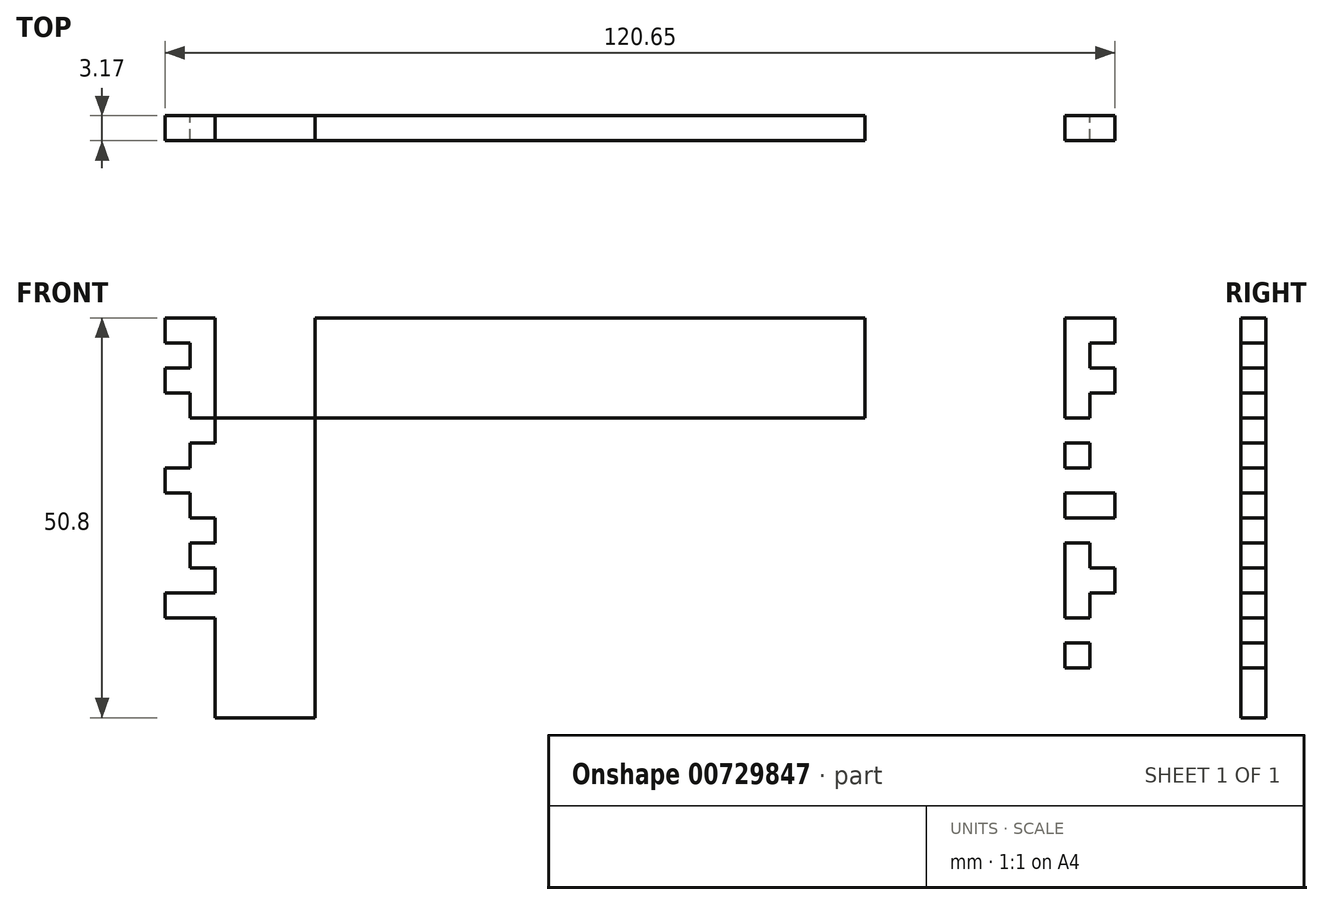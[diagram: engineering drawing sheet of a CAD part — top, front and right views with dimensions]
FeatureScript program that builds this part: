
annotation { "Feature Type Name" : "Feature", "Feature Type Description" : "" }
export const myFeature = defineFeature(function(context is Context, id is Id, definition is map)
    precondition{}
    {
        {
            var Q0;
            Q0=qCreatedBy(makeId("Front.planeOp"),FACE);
            var sketch = newSketch(context, id + "F0", { "sketchPlane" : qUnion([Q0])});
            skLineSegment(sketch, "E0.bottom", {"start": v(-86.22, 48.2) * mm, "end": v(34.43, 48.2) * mm});
            skLineSegment(sketch, "E0.top", {"start": v(-86.22, -2.6) * mm, "end": v(34.43, -2.6) * mm});
            skLineSegment(sketch, "E0.left", {"start": v(-86.22, 48.2) * mm, "end": v(-86.22, -2.6) * mm});
            skLineSegment(sketch, "E0.right", {"start": v(34.43, 48.2) * mm, "end": v(34.43, -2.6) * mm});
            skLineSegment(sketch, "E1.bottom", {"start": v(-86.22, 48.2) * mm, "end": v(-79.87, 48.2) * mm});
            skLineSegment(sketch, "E1.top", {"start": v(-86.22, -2.6) * mm, "end": v(-79.87, -2.6) * mm});
            skLineSegment(sketch, "E1.right", {"start": v(-79.87, 48.2) * mm, "end": v(-79.87, -2.6) * mm});
            skLineSegment(sketch, "E2.bottom", {"start": v(34.43, 48.2) * mm, "end": v(28.08, 48.2) * mm});
            skLineSegment(sketch, "E2.top", {"start": v(34.43, -2.6) * mm, "end": v(28.08, -2.6) * mm});
            skLineSegment(sketch, "E2.right", {"start": v(28.08, 48.2) * mm, "end": v(28.08, -2.6) * mm});
            skLineSegment(sketch, "E3.top", {"start": v(34.43, 41.85) * mm, "end": v(28.08, 41.85) * mm});
            skLineSegment(sketch, "E3.left", {"start": v(34.43, 48.2) * mm, "end": v(34.43, 41.85) * mm});
            skLineSegment(sketch, "E3.right", {"start": v(28.08, 48.2) * mm, "end": v(28.08, 41.85) * mm});
            skLineSegment(sketch, "E4.top", {"start": v(34.43, 35.5) * mm, "end": v(28.08, 35.5) * mm});
            skLineSegment(sketch, "E4.left", {"start": v(34.43, 48.2) * mm, "end": v(34.43, 35.5) * mm});
            skLineSegment(sketch, "E4.right", {"start": v(28.08, 48.2) * mm, "end": v(28.08, 35.5) * mm});
            skLineSegment(sketch, "E5.top", {"start": v(34.43, 22.8) * mm, "end": v(28.08, 22.8) * mm});
            skLineSegment(sketch, "E5.left", {"start": v(34.43, 48.2) * mm, "end": v(34.43, 22.8) * mm});
            skLineSegment(sketch, "E5.right", {"start": v(28.08, 48.2) * mm, "end": v(28.08, 22.8) * mm});
            skLineSegment(sketch, "E6.top", {"start": v(34.43, 16.45) * mm, "end": v(28.08, 16.45) * mm});
            skLineSegment(sketch, "E6.left", {"start": v(34.43, 48.2) * mm, "end": v(34.43, 16.45) * mm});
            skLineSegment(sketch, "E6.right", {"start": v(28.08, 48.2) * mm, "end": v(28.08, 16.45) * mm});
            skLineSegment(sketch, "E7.top", {"start": v(34.43, 10.1) * mm, "end": v(28.08, 10.1) * mm});
            skLineSegment(sketch, "E7.left", {"start": v(34.43, 48.2) * mm, "end": v(34.43, 10.1) * mm});
            skLineSegment(sketch, "E7.right", {"start": v(28.08, 48.2) * mm, "end": v(28.08, 10.1) * mm});
            skLineSegment(sketch, "E8.top", {"start": v(34.43, 3.75) * mm, "end": v(28.08, 3.75) * mm});
            skLineSegment(sketch, "E8.left", {"start": v(34.43, 48.2) * mm, "end": v(34.43, 3.75) * mm});
            skLineSegment(sketch, "E8.right", {"start": v(28.08, 48.2) * mm, "end": v(28.08, 3.75) * mm});
            skLineSegment(sketch, "E9.bottom", {"start": v(28.08, 48.2) * mm, "end": v(34.43, 48.2) * mm});
            skLineSegment(sketch, "E9.top", {"start": v(28.08, 29.15) * mm, "end": v(34.43, 29.15) * mm});
            skLineSegment(sketch, "E9.left", {"start": v(28.08, 48.2) * mm, "end": v(28.08, 29.15) * mm});
            skLineSegment(sketch, "E9.right", {"start": v(34.43, 48.2) * mm, "end": v(34.43, 29.15) * mm});
            skLineSegment(sketch, "E10.top", {"start": v(-86.22, 41.85) * mm, "end": v(-79.87, 41.85) * mm});
            skLineSegment(sketch, "E10.left", {"start": v(-86.22, 48.2) * mm, "end": v(-86.22, 41.85) * mm});
            skLineSegment(sketch, "E10.right", {"start": v(-79.87, 48.2) * mm, "end": v(-79.87, 41.85) * mm});
            skLineSegment(sketch, "E11.top", {"start": v(-86.22, 35.5) * mm, "end": v(-79.87, 35.5) * mm});
            skLineSegment(sketch, "E11.left", {"start": v(-86.22, 48.2) * mm, "end": v(-86.22, 35.5) * mm});
            skLineSegment(sketch, "E11.right", {"start": v(-79.87, 48.2) * mm, "end": v(-79.87, 35.5) * mm});
            skLineSegment(sketch, "E12.top", {"start": v(-86.22, 3.75) * mm, "end": v(-79.87, 3.75) * mm});
            skLineSegment(sketch, "E12.left", {"start": v(-86.22, 48.2) * mm, "end": v(-86.22, 3.75) * mm});
            skLineSegment(sketch, "E12.right", {"start": v(-79.87, 48.2) * mm, "end": v(-79.87, 3.75) * mm});
            skLineSegment(sketch, "E13.top", {"start": v(-86.22, 10.1) * mm, "end": v(-79.87, 10.1) * mm});
            skLineSegment(sketch, "E13.left", {"start": v(-86.22, 48.2) * mm, "end": v(-86.22, 10.1) * mm});
            skLineSegment(sketch, "E13.right", {"start": v(-79.87, 48.2) * mm, "end": v(-79.87, 10.1) * mm});
            skLineSegment(sketch, "E14.top", {"start": v(-86.22, 29.15) * mm, "end": v(-79.87, 29.15) * mm});
            skLineSegment(sketch, "E14.left", {"start": v(-86.22, 48.2) * mm, "end": v(-86.22, 29.15) * mm});
            skLineSegment(sketch, "E14.right", {"start": v(-79.87, 48.2) * mm, "end": v(-79.87, 29.15) * mm});
            skLineSegment(sketch, "E15.top", {"start": v(-86.22, 22.8) * mm, "end": v(-79.87, 22.8) * mm});
            skLineSegment(sketch, "E15.left", {"start": v(-86.22, 48.2) * mm, "end": v(-86.22, 22.8) * mm});
            skLineSegment(sketch, "E15.right", {"start": v(-79.87, 48.2) * mm, "end": v(-79.87, 22.8) * mm});
            skLineSegment(sketch, "E16.top", {"start": v(-86.22, 16.45) * mm, "end": v(-79.87, 16.45) * mm});
            skLineSegment(sketch, "E16.left", {"start": v(-86.22, 48.2) * mm, "end": v(-86.22, 16.45) * mm});
            skLineSegment(sketch, "E16.right", {"start": v(-79.87, 48.2) * mm, "end": v(-79.87, 16.45) * mm});
            skLineSegment(sketch, "E17", {"start": v(-79.87, 48.2) * mm, "end": v(-67.17, 48.2) * mm});
            skLineSegment(sketch, "E18", {"start": v(-67.17, 48.2) * mm, "end": v(-67.17, -2.6) * mm});
            skLineSegment(sketch, "E19", {"start": v(-86.22, 35.5) * mm, "end": v(34.43, 35.5) * mm});
            skLineSegment(sketch, "E20.bottom", {"start": v(-86.22, 48.2) * mm, "end": v(-83.05, 48.2) * mm});
            skLineSegment(sketch, "E20.top", {"start": v(-86.22, -2.6) * mm, "end": v(-83.05, -2.6) * mm});
            skLineSegment(sketch, "E20.right", {"start": v(-83.05, 48.2) * mm, "end": v(-83.05, -2.6) * mm});
            skLineSegment(sketch, "E21.bottom", {"start": v(-79.87, 48.2) * mm, "end": v(-86.22, 48.2) * mm});
            skLineSegment(sketch, "E21.top", {"start": v(-79.87, 45.02) * mm, "end": v(-86.22, 45.02) * mm});
            skLineSegment(sketch, "E21.left", {"start": v(-79.87, 48.2) * mm, "end": v(-79.87, 45.02) * mm});
            skLineSegment(sketch, "E21.right", {"start": v(-86.22, 48.2) * mm, "end": v(-86.22, 45.02) * mm});
            skLineSegment(sketch, "E22.bottom", {"start": v(-79.87, 41.85) * mm, "end": v(-86.22, 41.85) * mm});
            skLineSegment(sketch, "E22.top", {"start": v(-79.87, 38.67) * mm, "end": v(-86.22, 38.67) * mm});
            skLineSegment(sketch, "E22.left", {"start": v(-79.87, 41.85) * mm, "end": v(-79.87, 38.67) * mm});
            skLineSegment(sketch, "E22.right", {"start": v(-86.22, 41.85) * mm, "end": v(-86.22, 38.67) * mm});
            skLineSegment(sketch, "E23.bottom", {"start": v(-79.87, 35.5) * mm, "end": v(-86.22, 35.5) * mm});
            skLineSegment(sketch, "E23.top", {"start": v(-79.87, 32.32) * mm, "end": v(-86.22, 32.32) * mm});
            skLineSegment(sketch, "E23.left", {"start": v(-79.87, 35.5) * mm, "end": v(-79.87, 32.32) * mm});
            skLineSegment(sketch, "E23.right", {"start": v(-86.22, 35.5) * mm, "end": v(-86.22, 32.32) * mm});
            skLineSegment(sketch, "E24.bottom", {"start": v(-79.87, 29.15) * mm, "end": v(-86.22, 29.15) * mm});
            skLineSegment(sketch, "E24.top", {"start": v(-79.87, 25.97) * mm, "end": v(-86.22, 25.97) * mm});
            skLineSegment(sketch, "E24.left", {"start": v(-79.87, 29.15) * mm, "end": v(-79.87, 25.97) * mm});
            skLineSegment(sketch, "E24.right", {"start": v(-86.22, 29.15) * mm, "end": v(-86.22, 25.97) * mm});
            skLineSegment(sketch, "E25.bottom", {"start": v(-79.87, 3.75) * mm, "end": v(-86.22, 3.75) * mm});
            skLineSegment(sketch, "E25.top", {"start": v(-79.87, 0.57) * mm, "end": v(-86.22, 0.57) * mm});
            skLineSegment(sketch, "E25.left", {"start": v(-79.87, 3.75) * mm, "end": v(-79.87, 0.57) * mm});
            skLineSegment(sketch, "E25.right", {"start": v(-86.22, 3.75) * mm, "end": v(-86.22, 0.57) * mm});
            skLineSegment(sketch, "E26.bottom", {"start": v(-79.87, 22.8) * mm, "end": v(-86.22, 22.8) * mm});
            skLineSegment(sketch, "E26.top", {"start": v(-79.87, 19.62) * mm, "end": v(-86.22, 19.62) * mm});
            skLineSegment(sketch, "E26.left", {"start": v(-79.87, 22.8) * mm, "end": v(-79.87, 19.62) * mm});
            skLineSegment(sketch, "E26.right", {"start": v(-86.22, 22.8) * mm, "end": v(-86.22, 19.62) * mm});
            skLineSegment(sketch, "E27.bottom", {"start": v(-79.87, 16.45) * mm, "end": v(-86.22, 16.45) * mm});
            skLineSegment(sketch, "E27.top", {"start": v(-79.87, 13.27) * mm, "end": v(-86.22, 13.27) * mm});
            skLineSegment(sketch, "E27.left", {"start": v(-79.87, 16.45) * mm, "end": v(-79.87, 13.27) * mm});
            skLineSegment(sketch, "E27.right", {"start": v(-86.22, 16.45) * mm, "end": v(-86.22, 13.27) * mm});
            skLineSegment(sketch, "E28.bottom", {"start": v(-79.87, 10.1) * mm, "end": v(-86.22, 10.1) * mm});
            skLineSegment(sketch, "E28.top", {"start": v(-79.87, 6.92) * mm, "end": v(-86.22, 6.92) * mm});
            skLineSegment(sketch, "E28.left", {"start": v(-79.87, 10.1) * mm, "end": v(-79.87, 6.92) * mm});
            skLineSegment(sketch, "E28.right", {"start": v(-86.22, 10.1) * mm, "end": v(-86.22, 6.92) * mm});
            skLineSegment(sketch, "E29.bottom", {"start": v(34.43, 48.2) * mm, "end": v(31.25, 48.2) * mm});
            skLineSegment(sketch, "E29.top", {"start": v(34.43, -2.6) * mm, "end": v(31.25, -2.6) * mm});
            skLineSegment(sketch, "E29.right", {"start": v(31.25, 48.2) * mm, "end": v(31.25, -2.6) * mm});
            skLineSegment(sketch, "E30.top", {"start": v(28.08, 45.02) * mm, "end": v(34.43, 45.02) * mm});
            skLineSegment(sketch, "E30.left", {"start": v(28.08, 48.2) * mm, "end": v(28.08, 45.02) * mm});
            skLineSegment(sketch, "E30.right", {"start": v(34.43, 48.2) * mm, "end": v(34.43, 45.02) * mm});
            skLineSegment(sketch, "E31.bottom", {"start": v(28.08, 41.85) * mm, "end": v(34.43, 41.85) * mm});
            skLineSegment(sketch, "E31.top", {"start": v(28.08, 38.67) * mm, "end": v(34.43, 38.67) * mm});
            skLineSegment(sketch, "E31.left", {"start": v(28.08, 41.85) * mm, "end": v(28.08, 38.67) * mm});
            skLineSegment(sketch, "E31.right", {"start": v(34.43, 41.85) * mm, "end": v(34.43, 38.67) * mm});
            skLineSegment(sketch, "E32.bottom", {"start": v(28.08, 35.5) * mm, "end": v(34.43, 35.5) * mm});
            skLineSegment(sketch, "E32.top", {"start": v(28.08, 32.32) * mm, "end": v(34.43, 32.32) * mm});
            skLineSegment(sketch, "E32.left", {"start": v(28.08, 35.5) * mm, "end": v(28.08, 32.32) * mm});
            skLineSegment(sketch, "E32.right", {"start": v(34.43, 35.5) * mm, "end": v(34.43, 32.32) * mm});
            skLineSegment(sketch, "E33.top", {"start": v(28.08, 25.97) * mm, "end": v(34.43, 25.97) * mm});
            skLineSegment(sketch, "E33.left", {"start": v(28.08, 29.15) * mm, "end": v(28.08, 25.97) * mm});
            skLineSegment(sketch, "E33.right", {"start": v(34.43, 29.15) * mm, "end": v(34.43, 25.97) * mm});
            skLineSegment(sketch, "E34.bottom", {"start": v(28.08, 22.8) * mm, "end": v(34.43, 22.8) * mm});
            skLineSegment(sketch, "E34.top", {"start": v(28.08, 19.62) * mm, "end": v(34.43, 19.62) * mm});
            skLineSegment(sketch, "E34.left", {"start": v(28.08, 22.8) * mm, "end": v(28.08, 19.62) * mm});
            skLineSegment(sketch, "E34.right", {"start": v(34.43, 22.8) * mm, "end": v(34.43, 19.62) * mm});
            skLineSegment(sketch, "E35.bottom", {"start": v(28.08, 16.45) * mm, "end": v(34.43, 16.45) * mm});
            skLineSegment(sketch, "E35.top", {"start": v(28.08, 13.27) * mm, "end": v(34.43, 13.27) * mm});
            skLineSegment(sketch, "E35.left", {"start": v(28.08, 16.45) * mm, "end": v(28.08, 13.27) * mm});
            skLineSegment(sketch, "E35.right", {"start": v(34.43, 16.45) * mm, "end": v(34.43, 13.27) * mm});
            skLineSegment(sketch, "E36.bottom", {"start": v(28.08, 10.1) * mm, "end": v(34.43, 10.1) * mm});
            skLineSegment(sketch, "E36.top", {"start": v(28.08, 6.92) * mm, "end": v(34.43, 6.92) * mm});
            skLineSegment(sketch, "E36.left", {"start": v(28.08, 10.1) * mm, "end": v(28.08, 6.92) * mm});
            skLineSegment(sketch, "E36.right", {"start": v(34.43, 10.1) * mm, "end": v(34.43, 6.92) * mm});
            skLineSegment(sketch, "E37.bottom", {"start": v(28.08, 3.75) * mm, "end": v(34.43, 3.75) * mm});
            skLineSegment(sketch, "E37.top", {"start": v(28.08, 0.57) * mm, "end": v(34.43, 0.57) * mm});
            skLineSegment(sketch, "E37.left", {"start": v(28.08, 3.75) * mm, "end": v(28.08, 0.57) * mm});
            skLineSegment(sketch, "E37.right", {"start": v(34.43, 3.75) * mm, "end": v(34.43, 0.57) * mm});
            skLineSegment(sketch, "E38.bottom", {"start": v(28.08, 48.2) * mm, "end": v(15.38, 48.2) * mm});
            skLineSegment(sketch, "E38.top", {"start": v(28.08, 35.5) * mm, "end": v(15.38, 35.5) * mm});
            skLineSegment(sketch, "E38.right", {"start": v(15.38, 48.2) * mm, "end": v(15.38, 35.5) * mm});
            skCircle(sketch, "E39", {"center": v(15.38, 35.5) * mm, "radius": 6.35 * mm});
            skCircle(sketch, "E40", {"center": v(9.03, 35.5) * mm, "radius": 4.76 * mm});
            skLineSegment(sketch, "E41.bottom", {"start": v(15.38, 35.5) * mm, "end": v(2.68, 35.5) * mm});
            skLineSegment(sketch, "E41.top", {"start": v(15.38, 48.2) * mm, "end": v(2.68, 48.2) * mm});
            skLineSegment(sketch, "E41.left", {"start": v(15.38, 35.5) * mm, "end": v(15.38, 48.2) * mm});
            skLineSegment(sketch, "E41.right", {"start": v(2.68, 35.5) * mm, "end": v(2.68, 48.2) * mm});
            skSolve(sketch);
        }
        {
            var Q0;
            Q0=makeQuery(id+"F0.imprint","IMPRINT",FACE,{"disambiguationData":[TD([[makeQuery(id+"F0.imprint","IMPRINT",EDGE,{"derivedFrom":sQuery(id+"F0.wireOp",EDGE,"E1.top")}),1.0]])]});
            var Q1;
            Q1=makeQuery(id+"F0.imprint","IMPRINT",FACE,{"disambiguationData":[TD([[makeQuery(id+"F0.imprint","IMPRINT",EDGE,{"derivedFrom":sQuery(id+"F0.wireOp",EDGE,"E13.top")}),1.0]])]});
            var Q2;
            {var subQ6=sQuery(id+"F0.wireOp",EDGE,"E0.bottom");Q2=makeQuery(id+"F0.imprint","IMPRINT",FACE,{"disambiguationData":[TD([[makeQuery(id+"F0.imprint","IMPRINT",EDGE,{"derivedFrom":subQ6}),-1.0]])]});}
            var Q3;
            Q3=makeQuery(id+"F0.imprint","IMPRINT",FACE,{"disambiguationData":[TD([[makeQuery(id+"F0.imprint","IMPRINT",EDGE,{"derivedFrom":sQuery(id+"F0.wireOp",EDGE,"E2.top")}),-1.0]])]});
            var Q4;
            {var subQ0=sQuery(id+"F0.wireOp",EDGE,"E6.top");Q4=makeQuery(id+"F0.imprint","IMPRINT",FACE,{"disambiguationData":[TD([[makeQuery(id+"F0.imprint","IMPRINT",EDGE,{"derivedFrom":subQ0}),1.0]])]});}
            var Q5;
            {var subQ0=sQuery(id+"F0.wireOp",EDGE,"E5.top");Q5=makeQuery(id+"F0.imprint","IMPRINT",FACE,{"disambiguationData":[TD([[makeQuery(id+"F0.imprint","IMPRINT",EDGE,{"derivedFrom":subQ0}),-1.0]])]});}
            var Q6;
            {var subQ0=sQuery(id+"F0.wireOp",EDGE,"E3.top");Q6=makeQuery(id+"F0.imprint","IMPRINT",FACE,{"disambiguationData":[TD([[makeQuery(id+"F0.imprint","IMPRINT",EDGE,{"derivedFrom":subQ0}),1.0]])]});}
            var Q7;
            {var subQ0=sQuery(id+"F0.wireOp",EDGE,"E14.top");Q7=makeQuery(id+"F0.imprint","IMPRINT",FACE,{"disambiguationData":[TD([[makeQuery(id+"F0.imprint","IMPRINT",EDGE,{"derivedFrom":subQ0}),-1.0]])]});}
            var Q8;
            {var subQ0=sQuery(id+"F0.wireOp",EDGE,"E10.top");Q8=makeQuery(id+"F0.imprint","IMPRINT",FACE,{"disambiguationData":[TD([[makeQuery(id+"F0.imprint","IMPRINT",EDGE,{"derivedFrom":subQ0}),-1.0]])]});}
            var Q9;
            {var subQ1=sQuery(id+"F0.wireOp",EDGE,"E17");Q9=makeQuery(id+"F0.imprint","IMPRINT",FACE,{"disambiguationData":[TD([[makeQuery(id+"F0.imprint","IMPRINT",EDGE,{"derivedFrom":subQ1}),-1.0]])]});}
            var Q10;
            {var subQ5=sQuery(id+"F0.wireOp",EDGE,"E1.right");Q10=makeQuery(id+"F0.imprint","IMPRINT",FACE,{"disambiguationData":[TD([[makeQuery(id+"F0.imprint","IMPRINT",EDGE,{"derivedFrom":subQ5}),1.0]])]});}
            var Q11;
            {var subQ3=sQuery(id+"F0.wireOp",EDGE,"E2.right");Q11=makeQuery(id+"F0.imprint","IMPRINT",FACE,{"disambiguationData":[TD([[makeQuery(id+"F0.imprint","IMPRINT",EDGE,{"derivedFrom":subQ3}),-1.0]])]});}
            var Q12;
            {var subQ0=sQuery(id+"F0.wireOp",EDGE,"E21.top");var subQ5=sQuery(id+"F0.wireOp",EDGE,"E20.right");var subQ6=makeQuery(id+"F0.imprint","INTERSECT",VERTEX,{"derivedFrom":[subQ5,subQ0]});Q12=makeQuery(id+"F0.imprint","IMPRINT",FACE,{"disambiguationData":[TD([[makeQuery(id+"F0.imprint","IMPRINT",EDGE,{"disambiguationData":[TD([[subQ6,-1.0]])],"derivedFrom":subQ5}),1.0]])]});}
            var Q13;
            {var subQ3=sQuery(id+"F0.wireOp",EDGE,"E22.top");var subQ5=sQuery(id+"F0.wireOp",EDGE,"E20.right");var subQ6=makeQuery(id+"F0.imprint","INTERSECT",VERTEX,{"derivedFrom":[subQ5,subQ3]});Q13=makeQuery(id+"F0.imprint","IMPRINT",FACE,{"disambiguationData":[TD([[makeQuery(id+"F0.imprint","IMPRINT",EDGE,{"disambiguationData":[TD([[subQ6,-1.0]])],"derivedFrom":subQ5}),1.0]])]});}
            var Q14;
            {var subQ0=sQuery(id+"F0.wireOp",EDGE,"E23.top");var subQ5=sQuery(id+"F0.wireOp",EDGE,"E20.right");var subQ6=makeQuery(id+"F0.imprint","INTERSECT",VERTEX,{"derivedFrom":[subQ5,subQ0]});Q14=makeQuery(id+"F0.imprint","IMPRINT",FACE,{"disambiguationData":[TD([[makeQuery(id+"F0.imprint","IMPRINT",EDGE,{"disambiguationData":[TD([[subQ6,-1.0]])],"derivedFrom":subQ5}),1.0]])]});}
            var Q15;
            {var subQ0=sQuery(id+"F0.wireOp",EDGE,"E24.top");var subQ5=sQuery(id+"F0.wireOp",EDGE,"E20.right");var subQ6=makeQuery(id+"F0.imprint","INTERSECT",VERTEX,{"derivedFrom":[subQ5,subQ0]});Q15=makeQuery(id+"F0.imprint","IMPRINT",FACE,{"disambiguationData":[TD([[makeQuery(id+"F0.imprint","IMPRINT",EDGE,{"disambiguationData":[TD([[subQ6,-1.0]])],"derivedFrom":subQ5}),1.0]])]});}
            var Q16;
            {var subQ3=sQuery(id+"F0.wireOp",EDGE,"E26.top");var subQ5=sQuery(id+"F0.wireOp",EDGE,"E20.right");var subQ7=makeQuery(id+"F0.imprint","INTERSECT",VERTEX,{"derivedFrom":[subQ5,subQ3]});Q16=makeQuery(id+"F0.imprint","IMPRINT",FACE,{"disambiguationData":[TD([[makeQuery(id+"F0.imprint","IMPRINT",EDGE,{"disambiguationData":[TD([[subQ7,-1.0]])],"derivedFrom":subQ5}),1.0]])]});}
            var Q17;
            {var subQ0=sQuery(id+"F0.wireOp",EDGE,"E13.right");Q17=makeQuery(id+"F0.imprint","IMPRINT",FACE,{"disambiguationData":[TD([[makeQuery(id+"F0.imprint","IMPRINT",EDGE,{"derivedFrom":subQ0}),-1.0]])]});}
            var Q18;
            {var subQ0=sQuery(id+"F0.wireOp",EDGE,"E12.right");Q18=makeQuery(id+"F0.imprint","IMPRINT",FACE,{"disambiguationData":[TD([[makeQuery(id+"F0.imprint","IMPRINT",EDGE,{"derivedFrom":subQ0}),-1.0]])]});}
            var Q19;
            {var subQ3=sQuery(id+"F0.wireOp",EDGE,"E36.top");var subQ5=sQuery(id+"F0.wireOp",EDGE,"E29.right");var subQ6=makeQuery(id+"F0.imprint","INTERSECT",VERTEX,{"derivedFrom":[subQ5,subQ3]});Q19=makeQuery(id+"F0.imprint","IMPRINT",FACE,{"disambiguationData":[TD([[makeQuery(id+"F0.imprint","IMPRINT",EDGE,{"disambiguationData":[TD([[subQ6,-1.0]])],"derivedFrom":subQ5}),-1.0]])]});}
            var Q20;
            {var subQ0=sQuery(id+"F0.wireOp",EDGE,"E35.top");var subQ5=sQuery(id+"F0.wireOp",EDGE,"E29.right");var subQ6=makeQuery(id+"F0.imprint","INTERSECT",VERTEX,{"derivedFrom":[subQ5,subQ0]});Q20=makeQuery(id+"F0.imprint","IMPRINT",FACE,{"disambiguationData":[TD([[makeQuery(id+"F0.imprint","IMPRINT",EDGE,{"disambiguationData":[TD([[subQ6,-1.0]])],"derivedFrom":subQ5}),-1.0]])]});}
            var Q21;
            {var subQ0=sQuery(id+"F0.wireOp",EDGE,"E34.top");var subQ5=sQuery(id+"F0.wireOp",EDGE,"E29.right");var subQ6=makeQuery(id+"F0.imprint","INTERSECT",VERTEX,{"derivedFrom":[subQ5,subQ0]});Q21=makeQuery(id+"F0.imprint","IMPRINT",FACE,{"disambiguationData":[TD([[makeQuery(id+"F0.imprint","IMPRINT",EDGE,{"disambiguationData":[TD([[subQ6,-1.0]])],"derivedFrom":subQ5}),-1.0]])]});}
            var Q22;
            {var subQ0=sQuery(id+"F0.wireOp",EDGE,"E33.top");var subQ5=sQuery(id+"F0.wireOp",EDGE,"E29.right");var subQ6=makeQuery(id+"F0.imprint","INTERSECT",VERTEX,{"derivedFrom":[subQ5,subQ0]});Q22=makeQuery(id+"F0.imprint","IMPRINT",FACE,{"disambiguationData":[TD([[makeQuery(id+"F0.imprint","IMPRINT",EDGE,{"disambiguationData":[TD([[subQ6,-1.0]])],"derivedFrom":subQ5}),-1.0]])]});}
            var Q23;
            {var subQ3=sQuery(id+"F0.wireOp",EDGE,"E32.top");var subQ5=sQuery(id+"F0.wireOp",EDGE,"E29.right");var subQ6=makeQuery(id+"F0.imprint","INTERSECT",VERTEX,{"derivedFrom":[subQ5,subQ3]});Q23=makeQuery(id+"F0.imprint","IMPRINT",FACE,{"disambiguationData":[TD([[makeQuery(id+"F0.imprint","IMPRINT",EDGE,{"disambiguationData":[TD([[subQ6,-1.0]])],"derivedFrom":subQ5}),-1.0]])]});}
            var Q24;
            {var subQ3=sQuery(id+"F0.wireOp",EDGE,"E31.top");var subQ5=sQuery(id+"F0.wireOp",EDGE,"E29.right");var subQ6=makeQuery(id+"F0.imprint","INTERSECT",VERTEX,{"derivedFrom":[subQ5,subQ3]});Q24=makeQuery(id+"F0.imprint","IMPRINT",FACE,{"disambiguationData":[TD([[makeQuery(id+"F0.imprint","IMPRINT",EDGE,{"disambiguationData":[TD([[subQ6,-1.0]])],"derivedFrom":subQ5}),-1.0]])]});}
            var Q25;
            {var subQ0=sQuery(id+"F0.wireOp",EDGE,"E30.top");var subQ5=sQuery(id+"F0.wireOp",EDGE,"E29.right");var subQ6=makeQuery(id+"F0.imprint","INTERSECT",VERTEX,{"derivedFrom":[subQ5,subQ0]});Q25=makeQuery(id+"F0.imprint","IMPRINT",FACE,{"disambiguationData":[TD([[makeQuery(id+"F0.imprint","IMPRINT",EDGE,{"disambiguationData":[TD([[subQ6,-1.0]])],"derivedFrom":subQ5}),-1.0]])]});}
            var Q26;
            {var subQ3=sQuery(id+"F0.wireOp",EDGE,"E38.bottom");Q26=makeQuery(id+"F0.imprint","IMPRINT",FACE,{"disambiguationData":[TD([[makeQuery(id+"F0.imprint","IMPRINT",EDGE,{"derivedFrom":subQ3}),1.0]])]});}
            var Q27;
            {var subQ0=sQuery(id+"F0.wireOp",EDGE,"E41.top");Q27=makeQuery(id+"F0.imprint","IMPRINT",FACE,{"disambiguationData":[TD([[makeQuery(id+"F0.imprint","IMPRINT",EDGE,{"derivedFrom":subQ0}),1.0]])]});}
            extrude(context, id + "F1", {"entities" : qUnion([Q0, Q1, Q2, Q3, Q4, Q5, Q6, Q7, Q8, Q9, Q10, Q11, Q12, Q13, Q14, Q15, Q16, Q17, Q18, Q19, Q20, Q21, Q22, Q23, Q24, Q25, Q26, Q27]), "depth" : 3.17 * mm, "offsetDistance" : 25.4 * mm});
        }
    });
